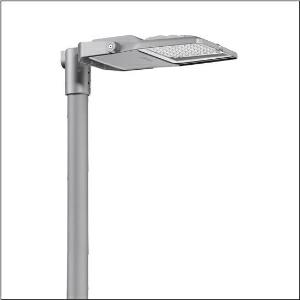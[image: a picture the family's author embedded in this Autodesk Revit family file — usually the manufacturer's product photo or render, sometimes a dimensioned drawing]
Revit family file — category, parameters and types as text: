
# Revit family: floodlight_fl_21_iq_mini___pl43_5xa7772d2a3a_1f0e
name_source: partatom
category: Lighting Fixtures
units: mm (PartAtom-declared; Revit-internal decimal feet)

## family parameters
Cut with Voids When Loaded = No
Host = Face
Light Source = No
Part Type = Normal
Room Calculation Point = No
Round Connector Dimension = Use Diameter
Shared = No

## types (1)
- --- (1 x LED, 18290 lm, 143 W, 3000K)
    Apparent Load = 143 VA
    CIE Flux Codes = 27 78 99 100 100
    Color Rendering = 70
    Color Temperature = 3000K
    Default Elevation = 1800 mm
    Description = Floodlight FL 21 iQ mini, floodlight, primary light control with lens, of PMMA, primary optical cover: protective disc, of toughened safety glass, transparent, light distribution: PL43, light emission: direct distribution, installation type: surface-mounted, LED, High Power LED, rated luminous flux: 18.290lm, luminous efficacy: 128lm/W, light colour: 730, colour temperature: 3000K, control: Auto-Match, Temp-Guard, Night-Set, Smart-Wire, Desk-Remote (wireless, voltage-free reading and setting of iQ features in the workshop via application-optimized NFC function/RFID function), optimised constant luminous flux control (CLO 2.0), Light-Fading, Lumen-Switch, with terminal, 6-pole, mains connection: 220..240V, AC, 50/60Hz, start of lifetime: 143W, end of service life: 152W, reduction: 61W, luminaire housing, of diecast aluminium, powder-coated, Siteco® metallic grey (DB 702S), corrosivity category C5 mid according to DIN EN ISO 12944, sealing non-destructively replaceable, please order mast flange separately, mast bracket, of steel, galvanised, powder-coated, protection rating (complete): IP66, insulation class (complete): insulation class II (safety insulation), certification: CE, ENEC, VDE, protection symbol: D, impact resistance: IK08, permissible operating ambient temperature: -40..+40°C, permissible operating ambient temperature for outdoor applications: -40..+50°C, standard: DIN EN 12944, LABS conformity tested according to VDMA 24364:2018-05, packaging unit: 1 piece

Light Distribution: PL43
    Height = 70 mm
    Lamp = 1 x LED
    Lamp Light Flux = 18290 lm
    Lamp Power = 143 W
    Lamp count = 1
    Length = 485 mm
    Luminous efficacy = 128 lm/W
    Manufacturer = Siteco
    ModVariant = No
    Model = 5XA7772D2A3A
    Number of Poles = 1
    OnlyDefault = Yes
    Power Factor = 1
    Product Name = Floodlight FL 21 iQ mini | PL43
    Product group = floodlight | pylon annexe
    ProductGroupID = 6200
    Protection Class = Protection class II
    Protection Degree = IP 66
    RLX_Detail_Level = 1
    RLX_Emergency_Light_Flux = 0 lm
    RLX_Emergency_Type = 0
    RLX_Emergency_Type_DB = No
    RlxData = <blob elided: 101421 chars, md5=bf0720e2>
    Socket = socket
    Standby Power = 0 W
    System Light Flux = 18290 lm
    System Power = 143 W
    Type Comments = factory setting: luminous flux: 100 % | dim-lin: 254 | 730 mA
    Type Image = l_1007125.jpg
    URL = http://relux.com
    VarID = @adj_131957
    Voltage = 0 V
    Weight = 0.00 kg
    Width = 337 mm

## geometry (parser evidence)
native form markers: Blend x4, Sweep x12
no freeform markers — native parametric forms only
